# Revit family: Zilenzio + Allsteel - Dezibel Print - Rectangle - 30mm
name_source: partatom
category: Generic Models
revit_build: Autodesk Revit 2017 (Build: 20160225_1515(x64)
units: mm (PartAtom-declared; Revit-internal decimal feet)

## family parameters
Can host rebar = No
Cut with Voids When Loaded = No
Host = Face
Part Type = Normal
Room Calculation Point = No
Round Connector Dimension = Use Diameter
Shared = No

## types (12) — shared parameters
Default Elevation = 4' - 0"
Depth = 0' - 2"
Manufacturer = Zilenzio + Allsteel
URL = www.zilenzio.com / www.allsteeloffice.com

## per-type parameters (varying)
| type | Description | Height | Model | Width |
| 900 x 600 mm | Zilenzio + Allsteel - Dezibel Print - Rectangle - 30mm x 900mm x 600mm | 1' - 11 19/32" | 63-0609 | 2' - 11 13/32" |
| 1200 x 450 mm | Zilenzio + Allsteel - Dezibel Print - Rectangle - 30mm x 1200mm x 450mm | 1' - 5 11/16" | 63-0412 | 3' - 11 3/16" |
| 1200 x 600 mm | Zilenzio + Allsteel - Dezibel Print - Rectangle - 30mm x 1200mm x 600mm | 1' - 11 19/32" | 63-0612 | 3' - 11 3/16" |
| 1200 x 800 mm | Zilenzio + Allsteel - Dezibel Print - Rectangle - 30mm x 1200mm x 800mm | 2' - 7 1/2" | 63-0812 | 3' - 11 3/16" |
| 1800 x 600 mm | Zilenzio + Allsteel - Dezibel Print - Rectangle - 30mm x 1800mm x 600mm | 1' - 11 19/32" | 63-0618 | 5' - 10 29/32" |
| 1800 x 800 mm | Zilenzio + Allsteel - Dezibel Print - Rectangle - 30mm x 1800mm x 800mm | 2' - 7 1/2" | 63-0818 | 5' - 10 29/32" |
| 450 x 1200 mm | Zilenzio + Allsteel - Dezibel Print - Rectangle - 30mm x 450mm x 1200mm | 3' - 11 3/16" | 63-1204 | 1' - 5 11/16" |
| 600 x 1200 mm | Zilenzio + Allsteel - Dezibel Print - Rectangle - 30mm x 600mm x 1200mm | 3' - 11 3/16" | 63-1206 | 1' - 11 19/32" |
| 800 x 1200 mm | Zilenzio + Allsteel - Dezibel Print - Rectangle - 30mm x 800mm x 1200mm | 3' - 11 3/16" | 63-1208 | 2' - 7 1/2" |
| 600 x 1800 mm | Zilenzio + Allsteel - Dezibel Print - Rectangle - 30mm x 600mm x 1800mm | 5' - 10 29/32" | 63-1806 | 1' - 11 19/32" |
| 800 x 1800 mm | Zilenzio + Allsteel - Dezibel Print - Rectangle - 30mm x 800mm x 1800mm | 5' - 10 29/32" | 63-1808 | 2' - 7 1/2" |
| 600 x 900 mm | Zilenzio + Allsteel - Dezibel Print - Rectangle - 30mm x 600mm x 900mm | 2' - 11 13/32" | 63-0906 | 1' - 11 19/32" |

## geometry (parser evidence)
native form markers: Sweep x2
no freeform markers — native parametric forms only
